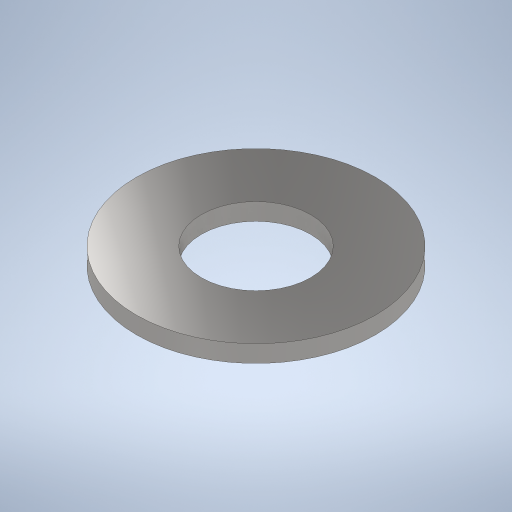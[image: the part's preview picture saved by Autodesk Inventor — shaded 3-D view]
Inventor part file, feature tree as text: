
AUTODESK INVENTOR PART (.ipt)
format: ipt  version: 2024.2 (Build 282272000, 272)  size: 235,520 bytes
history: native  units: in
note: dims shown in document units (in); Inventor stores cm internally (conversion verified against a paired STEP export)
features: extrude x1, sketch x1
ambient origin geometry x8: Origin, YZ Plane, XZ Plane, XY Plane, X Axis, Y Axis, Z Axis, Center Point
bodies: Solid1 (feature_tree)
feature tree (2):
  extrude  "Extrusion1"  Depth=0.0197in
  sketch  "Sketch1"  dims[d0=0.2756in d1=0.126in d2=0.0197in d3=0.0in]
